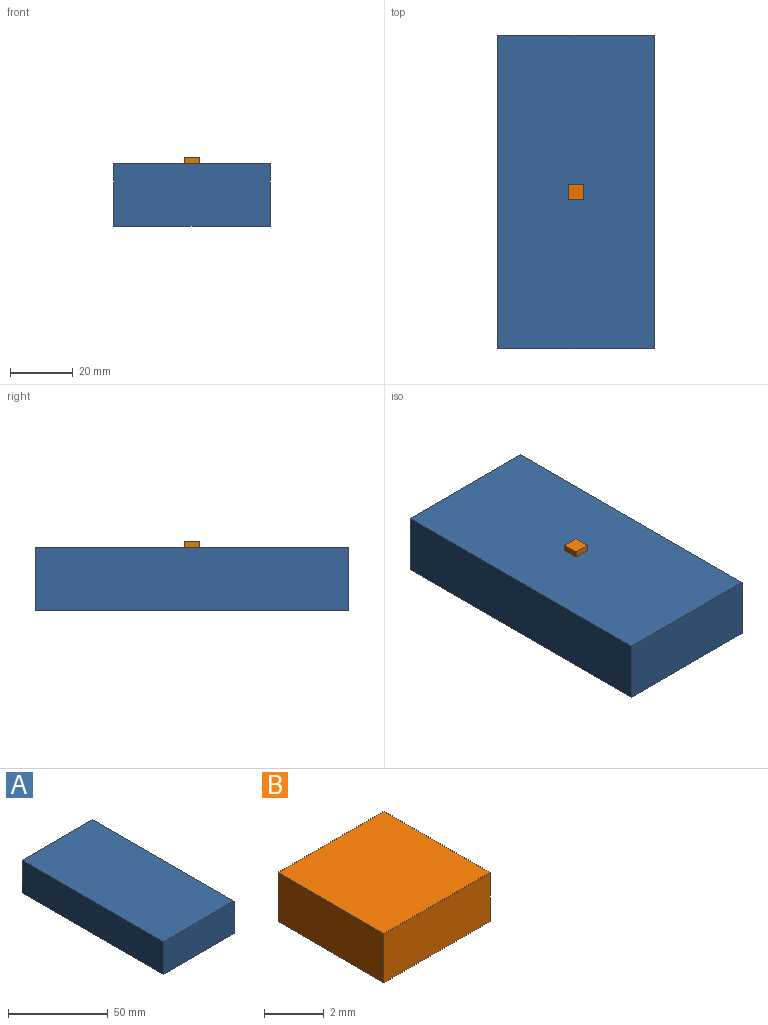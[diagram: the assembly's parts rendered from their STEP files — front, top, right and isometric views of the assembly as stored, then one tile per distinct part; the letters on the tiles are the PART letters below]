
ASSEMBLY  parts=2 mates=1
PART A: 6 faces, bbox 50x100x20 mm
  f0: plane 100x50mm, normal (0,0,1), area 5000mm2, adj f1,f3,f4,f5
  f1: plane 100x20mm, normal (-1,0,0), area 2000mm2, adj f0,f2,f4,f5
  f2: plane 100x50mm, normal (0,0,-1), area 5000mm2, adj f1,f3,f4,f5
  f3: plane 100x20mm, normal (1,0,0), area 2000mm2, adj f0,f2,f4,f5
  f4: plane 50x20mm, normal (0,-1,0), area 1000mm2, adj f0,f1,f2,f3
  f5: plane 50x20mm, normal (0,1,0), area 1000mm2, adj f0,f1,f2,f3
PART B: 6 faces, bbox 5x5x2 mm
  f0: plane 5x2mm, normal (0,-1,0), area 10mm2, adj f1,f3,f4,f5
  f1: plane 5x2mm, normal (1,0,0), area 10mm2, adj f0,f2,f4,f5
  f2: plane 5x2mm, normal (0,1,0), area 10mm2, adj f1,f3,f4,f5
  f3: plane 5x2mm, normal (-1,0,0), area 10mm2, adj f0,f2,f4,f5
  f4: plane 5x5mm, normal (0,0,1), area 25mm2, adj f0,f1,f2,f3
  f5: plane 5x5mm, normal (0,0,-1), area 25mm2, adj f0,f1,f2,f3
PLACE A t=(-65.37,18.84,-0.13)mm
PLACE B t=(-65.37,-31.16,9.87)mm
MATE fastened A.f0 <-> B.f5  axis (0,0,1) through (-65.37,-31.16,9.87)mm
